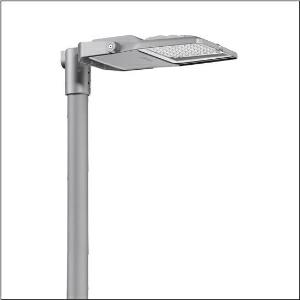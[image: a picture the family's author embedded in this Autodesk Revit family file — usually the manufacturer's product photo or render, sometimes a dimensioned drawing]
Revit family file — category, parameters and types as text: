
# Revit family: floodlight_fl_21_iq_mini___pl64_5xa7772d4e3a_9d14
name_source: partatom
category: Lighting Fixtures
units: mm (PartAtom-declared; Revit-internal decimal feet)

## family parameters
Cut with Voids When Loaded = No
Host = Face
Light Source = No
Part Type = Normal
Room Calculation Point = No
Round Connector Dimension = Use Diameter
Shared = No

## types (1)
- --- (1 x LED, 17970 lm, 143 W, 4000K)
    Apparent Load = 143 VA
    CIE Flux Codes = 28 80 98 100 100
    Color Rendering = 70
    Color Temperature = 4000K
    Default Elevation = 1800 mm
    Description = Floodlight FL 21 iQ mini, floodlight, primary light control with lens, of PMMA, primary optical cover: protective disc, of toughened safety glass, transparent, light distribution: PL64, light emission: direct distribution, installation type: surface-mounted, LED, High Power LED, rated luminous flux: 17.970lm, luminous efficacy: 126lm/W, light colour: 740, colour temperature: 4000K, control: Auto-Match, Temp-Guard, Night-Set, Smart-Wire, Desk-Remote (wireless, voltage-free reading and setting of iQ features in the workshop via application-optimized NFC function/RFID function), optimised constant luminous flux control (CLO 2.0), Light-Fading, Lumen-Switch, with terminal, 6-pole, mains connection: 220..240V, AC, 50/60Hz, start of lifetime: 143W, end of service life: 152W, reduction: 61W, luminaire housing, of diecast aluminium, powder-coated, Siteco® metallic grey (DB 702S), corrosivity category C5 mid according to DIN EN ISO 12944, sealing non-destructively replaceable, please order mast flange separately, mast bracket, of steel, galvanised, powder-coated, protection rating (complete): IP66, insulation class (complete): insulation class II (safety insulation), certification: CE, ENEC, VDE, protection symbol: D, impact resistance: IK08, permissible operating ambient temperature: -40..+40°C, permissible operating ambient temperature for outdoor applications: -40..+50°C, standard: DIN EN 12944, LABS conformity tested according to VDMA 24364:2018-05, packaging unit: 1 piece

Light Distribution: PL64
    Height = 70 mm
    Lamp = 1 x LED
    Lamp Light Flux = 17970 lm
    Lamp Power = 143 W
    Lamp count = 1
    Length = 485 mm
    Luminous efficacy = 126 lm/W
    Manufacturer = Siteco
    ModVariant = No
    Model = 5XA7772D4E3A
    Number of Poles = 1
    OnlyDefault = Yes
    Power Factor = 1
    Product Name = Floodlight FL 21 iQ mini | PL64
    Product group = floodlight | pylon annexe
    ProductGroupID = 6200
    Protection Class = Protection class II
    Protection Degree = IP 66
    RLX_Detail_Level = 1
    RLX_Emergency_Light_Flux = 0 lm
    RLX_Emergency_Type = 0
    RLX_Emergency_Type_DB = No
    RlxData = <blob elided: 101521 chars, md5=cfb5facd>
    Socket = socket
    Standby Power = 0 W
    System Light Flux = 17970 lm
    System Power = 143 W
    Type Comments = factory setting: luminous flux: 100 % | dim-lin: 254 | 730 mA
    Type Image = l_1007125.jpg
    URL = http://relux.com
    VarID = @adj_097949
    Voltage = 0 V
    Weight = 0.00 kg
    Width = 337 mm

## geometry (parser evidence)
native form markers: Blend x4, Sweep x11
no freeform markers — native parametric forms only
